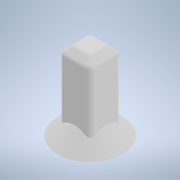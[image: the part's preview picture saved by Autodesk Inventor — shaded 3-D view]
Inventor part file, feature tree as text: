
AUTODESK INVENTOR PART (.ipt)
format: ipt  version: 2022 (Build 260153000, 153)  size: 150,528 bytes
history: native  units: mm
features: extrude x2, chamfer x2, sketch x2, other x1, fillet x1
ambient origin geometry x8: Origin, YZ Plane, XZ Plane, XY Plane, X Axis, Y Axis, Z Axis, Center Point
bodies: Body1 (feature_tree)
feature tree (8):
  other  "Твердое тело1"
  extrude  "Выдавливание1"  Depth=9.9mm
  chamfer  "Фаска1"  Distance=4.95mm
  extrude  "Выдавливание2"  Depth=4.95mm TaperAngle=45.0deg
  chamfer  "Фаска2"  Distance=4.75mm
  fillet  "Сопряжение1"  Radius=4.75mm
  sketch  "Эскиз1"
  sketch  "Эскиз2"
